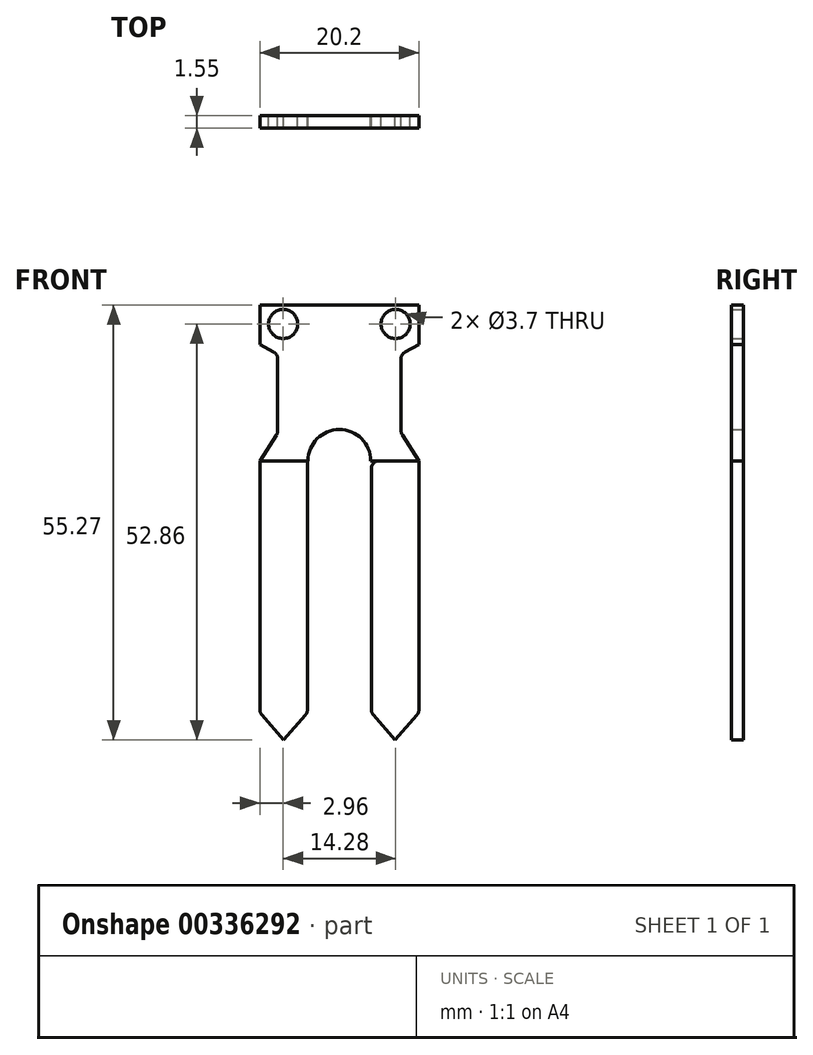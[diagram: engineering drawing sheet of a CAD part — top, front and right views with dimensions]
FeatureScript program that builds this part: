
annotation { "Feature Type Name" : "Feature", "Feature Type Description" : "" }
export const myFeature = defineFeature(function(context is Context, id is Id, definition is map)
    precondition{}
    {
        {
            var Q0;
            Q0=qCreatedBy(makeId("Front.planeOp"),FACE);
            var sketch = newSketch(context, id + "F0", { "sketchPlane" : qUnion([Q0])});
            skLineSegment(sketch, "E0.bottom", {"start": v(-10.1, 9.9) * mm, "end": v(10.1, 9.9) * mm});
            skPoint(sketch, "E0.middle", {"position": v(0, 0) * mm});
            skCircle(sketch, "E1", {"center": v(-7.14, 7.49) * mm, "radius": 1.85 * mm});
            skLineSegment(sketch, "E2", {"start": v(-10.1, -9.9) * mm, "end": v(-3.98, -9.9) * mm});
            skLineSegment(sketch, "E3", {"start": v(10.1, -9.9) * mm, "end": v(3.98, -9.9) * mm});
            skLineSegment(sketch, "E4", {"start": v(-3.98, -9.9) * mm, "end": v(3.98, -9.9) * mm, "construction": true});
            skArc(sketch, "E5", {"start": v(3.98, -9.9) * mm, "mid": v(0, -5.92) * mm, "end": v(-3.98, -9.9) * mm});
            skLineSegment(sketch, "E6", {"start": v(0, -9.9) * mm, "end": v(0, -5.92) * mm, "construction": true});
            skLineSegment(sketch, "E7.bottom", {"start": v(-10.1, -9.9) * mm, "end": v(-4.06, -9.9) * mm});
            skLineSegment(sketch, "E7.left", {"start": v(-10.1, -9.9) * mm, "end": v(-10.1, -41.88) * mm});
            skLineSegment(sketch, "E7.right", {"start": v(-4.06, -9.9) * mm, "end": v(-4.06, -41.88) * mm});
            skLineSegment(sketch, "E8", {"start": v(-10.1, -41.88) * mm, "end": v(-7.08, -45.37) * mm});
            skLineSegment(sketch, "E9", {"start": v(-7.08, -45.37) * mm, "end": v(-4.06, -41.88) * mm});
            skLineSegment(sketch, "E10", {"start": v(0, 9.9) * mm, "end": v(0, -46.77) * mm, "construction": true});
            skLineSegment(sketch, "E11.MirrorCS", {"start": v(10.1, -9.9) * mm, "end": v(4.06, -9.9) * mm});
            skLineSegment(sketch, "E12.MirrorCS", {"start": v(10.1, -9.9) * mm, "end": v(10.1, -41.88) * mm});
            skLineSegment(sketch, "E13.MirrorCS", {"start": v(4.06, -9.9) * mm, "end": v(4.06, -41.88) * mm});
            skLineSegment(sketch, "E14.MirrorCS", {"start": v(10.1, -41.88) * mm, "end": v(7.08, -45.37) * mm});
            skLineSegment(sketch, "E15.MirrorCS", {"start": v(7.08, -45.37) * mm, "end": v(4.06, -41.88) * mm});
            skCircle(sketch, "E16.MirrorC", {"center": v(7.14, 7.49) * mm, "radius": 1.85 * mm});
            skLineSegment(sketch, "E17", {"start": v(-10.1, 9.9) * mm, "end": v(-10.1, 4.87) * mm});
            skLineSegment(sketch, "E18", {"start": v(-10.1, 4.87) * mm, "end": v(-7.83, 3.66) * mm});
            skLineSegment(sketch, "E19", {"start": v(-7.83, 3.66) * mm, "end": v(-7.83, -6.34) * mm});
            skLineSegment(sketch, "E20", {"start": v(-10.1, -9.9) * mm, "end": v(-7.83, -6.34) * mm});
            skLineSegment(sketch, "E21.MirrorCS", {"start": v(10.1, 4.87) * mm, "end": v(7.83, 3.66) * mm});
            skLineSegment(sketch, "E22.MirrorCS", {"start": v(10.1, 9.9) * mm, "end": v(10.1, 4.87) * mm});
            skLineSegment(sketch, "E23.MirrorCS", {"start": v(10.1, -9.9) * mm, "end": v(7.83, -6.34) * mm});
            skLineSegment(sketch, "E24.MirrorCS", {"start": v(7.83, 3.66) * mm, "end": v(7.83, -6.34) * mm});
            skSolve(sketch);
        }
        {
            var Q0;
            {var subQ4=sQuery(id+"F0.wireOp",EDGE,"E7.left");Q0=makeQuery(id+"F0.imprint","IMPRINT",FACE,{"disambiguationData":[TD([[makeQuery(id+"F0.imprint","IMPRINT",EDGE,{"derivedFrom":subQ4}),1.0]])]});}
            var Q1;
            {var subQ0=sQuery(id+"F0.wireOp",EDGE,"E12.MirrorCS");Q1=makeQuery(id+"F0.imprint","IMPRINT",FACE,{"disambiguationData":[TD([[makeQuery(id+"F0.imprint","IMPRINT",EDGE,{"derivedFrom":subQ0}),-1.0]])]});}
            var Q2;
            Q2=makeQuery(id+"F0.imprint","IMPRINT",FACE,{"disambiguationData":[TD([[makeQuery(id+"F0.imprint","IMPRINT",EDGE,{"derivedFrom":sQuery(id+"F0.wireOp",EDGE,"E0.bottom")}),-1.0]])]});
            var Q3;
            {var subQ0=sQuery(id+"F0.wireOp",EDGE,"E11.MirrorCS");Q3=makeQuery(id+"F0.imprint","IMPRINT",FACE,{"disambiguationData":[TD([[makeQuery(id+"F0.imprint","IMPRINT",EDGE,{"derivedFrom":subQ0}),1.0]])]});}
            extrude(context, id + "F1", {"entities" : qUnion([Q0, Q1, Q2, Q3]), "depth" : 1.55 * mm});
        }
        {
            var Q0;
            Q0=makeQuery(id+"F1.opExtrude","SWEPT_EDGE",EDGE,{"disambiguationData":[OSD([sQuery(id+"F0.wireOp",EDGE,"E21.MirrorCS"),sQuery(id+"F0.wireOp",EDGE,"E24.MirrorCS")])]});
            var Q1;
            Q1=makeQuery(id+"F1.opExtrude","SWEPT_EDGE",EDGE,{"disambiguationData":[OSD([sQuery(id+"F0.wireOp",EDGE,"E23.MirrorCS"),sQuery(id+"F0.wireOp",EDGE,"E24.MirrorCS")])]});
            var Q2;
            Q2=makeQuery(id+"F1.opExtrude","SWEPT_EDGE",EDGE,{"disambiguationData":[OSD([sQuery(id+"F0.wireOp",EDGE,"E18"),sQuery(id+"F0.wireOp",EDGE,"E19")])]});
            var Q3;
            Q3=makeQuery(id+"F1.opExtrude","SWEPT_EDGE",EDGE,{"disambiguationData":[OSD([sQuery(id+"F0.wireOp",EDGE,"E19"),sQuery(id+"F0.wireOp",EDGE,"E20")])]});
            var Q4;
            Q4=makeQuery(id+"F1.opExtrude","SWEPT_EDGE",EDGE,{"disambiguationData":[OSD([sQuery(id+"F0.wireOp",EDGE,"E7.left"),sQuery(id+"F0.wireOp",EDGE,"E8")])]});
            var Q5;
            Q5=makeQuery(id+"F1.opExtrude","SWEPT_EDGE",EDGE,{"disambiguationData":[OSD([sQuery(id+"F0.wireOp",EDGE,"E7.right"),sQuery(id+"F0.wireOp",EDGE,"E9")])]});
            var Q6;
            Q6=makeQuery(id+"F1.opExtrude","SWEPT_EDGE",EDGE,{"disambiguationData":[OSD([sQuery(id+"F0.wireOp",EDGE,"E13.MirrorCS"),sQuery(id+"F0.wireOp",EDGE,"E15.MirrorCS")])]});
            var Q7;
            Q7=makeQuery(id+"F1.opExtrude","SWEPT_EDGE",EDGE,{"disambiguationData":[OSD([sQuery(id+"F0.wireOp",EDGE,"E12.MirrorCS"),sQuery(id+"F0.wireOp",EDGE,"E14.MirrorCS")])]});
            fillet(context, id + "F2", {"entities" : qUnion([Q0, Q1, Q2, Q3, Q4, Q5, Q6, Q7]), "radius" : 1 * mm, "tangentPropagation" : true, "allowEdgeOverflow" : false});
        }
    });
